# Revit family: HCXL
name_source: partatom
category: Attrezzature speciali
revit_build: Autodesk Revit 2016 (Build: 20150714_1515(x64)
units: mm (PartAtom-declared; Revit-internal decimal feet)

## family parameters
Basato su piano di lavoro = No
Condiviso = No
Punto di calcolo locali = No
Quota connettore circolare = Usa diametro
Sempre verticale = Sì
Taglio con vuoti quando caricato = No
Tipo di parte = Normale

## types (3) — shared parameters
230 Volt = No
400 Volt = Sì
Air gap = Sì
Capacity factor = 80.00%
Clearance = 530 mm
Electrical supply = 400 V
Height = 1637 mm  [stored 5.37073 ft]
Length = 717 mm
Output racks/h = 40
Rack size = 500 x 600
Rinse water consumption = 2.5 L
Sensible Heat = 2.10 kW
Tank drain = 35 mm  [stored 0.114829 ft]
Water inlet = 1"
Width = 740 mm  [stored 2.42782 ft]

## per-type parameters (varying)
| type | Apparent power | CRC | Installed Load | Latent Heat | Overall size | Total absorption | Water softener |
| HCXL R | 8960 VA | No | 11.2 kW | 2.59 kW | 1970 mm | 18 A | No |
| HCXL RA | 8960 VA | No | 11.2 kW | 2.59 kW | 1970 mm | 18 A | Sì |
| HCXL RA- CRC | 9760 VA | Sì | 12.2 kW | 0 kW | 2076 mm | 20 A | Sì |

note: [stored X ft] marks values corroborated as IEEE doubles in the binary element streams (Revit-internal decimal feet)
